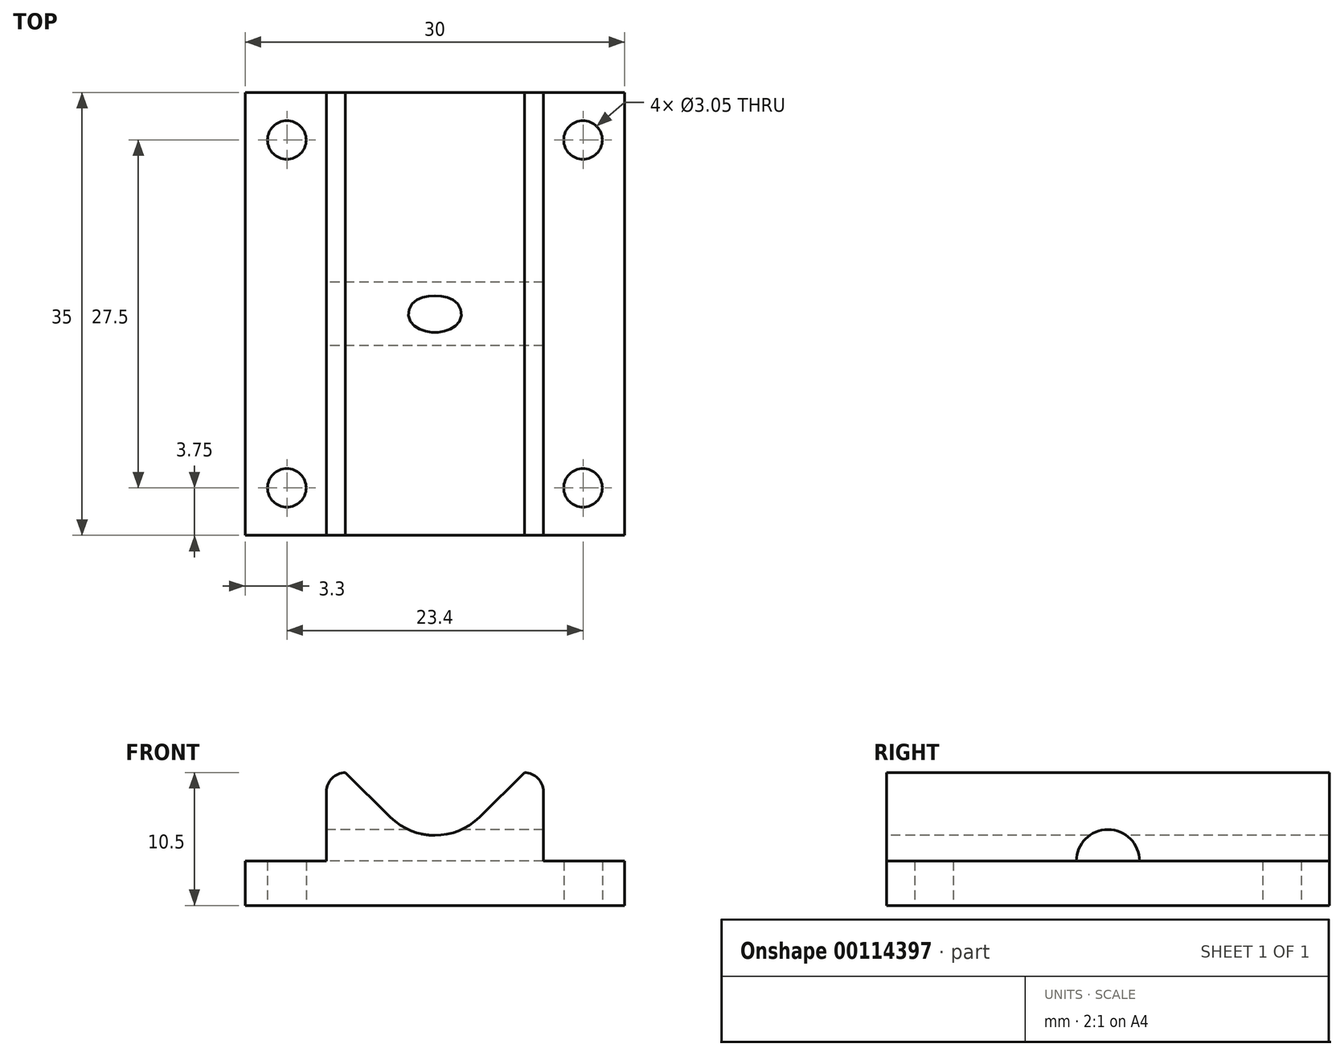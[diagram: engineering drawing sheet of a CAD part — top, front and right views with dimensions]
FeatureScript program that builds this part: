
annotation { "Feature Type Name" : "Feature", "Feature Type Description" : "" }
export const myFeature = defineFeature(function(context is Context, id is Id, definition is map)
    precondition{}
    {
        {
            var Q0;
            Q0=qCreatedBy(makeId("Top.planeOp"),FACE);
            var sketch = newSketch(context, id + "F0", { "sketchPlane" : qUnion([Q0])});
            skLineSegment(sketch, "E0.bottom", {"start": v(0, 0) * mm, "end": v(30, 0) * mm});
            skLineSegment(sketch, "E0.top", {"start": v(0, 35) * mm, "end": v(30, 35) * mm});
            skLineSegment(sketch, "E0.left", {"start": v(0, 0) * mm, "end": v(0, 35) * mm});
            skLineSegment(sketch, "E0.right", {"start": v(30, 0) * mm, "end": v(30, 35) * mm});
            skSolve(sketch);
        }
        {
            var Q0;
            Q0=makeQuery(id+"F0.imprint","IMPRINT",FACE,{"disambiguationData":[TD([[makeQuery(id+"F0.imprint","IMPRINT",EDGE,{"derivedFrom":sQuery(id+"F0.wireOp",EDGE,"E0.bottom")}),1.0]])]});
            extrude(context, id + "F1", {"entities" : qUnion([Q0]), "depth" : 13 * mm});
        }
        {
            var Q0;
            Q0=makeQuery(id+"F1.opExtrude","SWEPT_FACE",FACE,{"disambiguationData":[OSD([sQuery(id+"F0.wireOp",EDGE,"E0.bottom")])]});
            var sketch = newSketch(context, id + "F2", { "sketchPlane" : qUnion([Q0])});
            skLineSegment(sketch, "E1", {"start": v(15, 13) * mm, "end": v(15, 0) * mm, "construction": true});
            skCircle(sketch, "E2", {"center": v(15, 13) * mm, "radius": 6.75 * mm, "construction": true});
            skLineSegment(sketch, "E3", {"start": v(0, 3.5) * mm, "end": v(3.9, 3.5) * mm});
            skLineSegment(sketch, "E4", {"start": v(3.9, 3.5) * mm, "end": v(3.9, 13) * mm});
            skLineSegment(sketch, "E5", {"start": v(3.9, 13) * mm, "end": v(0, 13) * mm});
            skLineSegment(sketch, "E6", {"start": v(0, 13) * mm, "end": v(0, 3.5) * mm});
            skLineSegment(sketch, "E7", {"start": v(3.9, 13) * mm, "end": v(5.4, 13) * mm, "construction": true});
            skLineSegment(sketch, "E8", {"start": v(5.4, 13) * mm, "end": v(15, 3.5) * mm});
            skLineSegment(sketch, "E9", {"start": v(15, 3.5) * mm, "end": v(3.9, 3.5) * mm, "construction": true});
            skLineSegment(sketch, "E10", {"start": v(5.4, 13) * mm, "end": v(15, 13) * mm});
            skLineSegment(sketch, "E11", {"start": v(15, 3.5) * mm, "end": v(15, 13) * mm, "construction": true});
            skLineSegment(sketch, "E12.MirrorCS", {"start": v(15, 13) * mm, "end": v(15, 26) * mm, "construction": true});
            skLineSegment(sketch, "E13.MirrorCS", {"start": v(24.6, 13) * mm, "end": v(15, 13) * mm});
            skLineSegment(sketch, "E14.MirrorCS", {"start": v(24.6, 13) * mm, "end": v(15, 3.5) * mm});
            skLineSegment(sketch, "E15.MirrorCS", {"start": v(26.1, 3.5) * mm, "end": v(26.1, 13) * mm});
            skLineSegment(sketch, "E16.MirrorCS", {"start": v(26.1, 13) * mm, "end": v(30, 13) * mm});
            skLineSegment(sketch, "E17.MirrorCS", {"start": v(30, 13) * mm, "end": v(30, 3.5) * mm});
            skLineSegment(sketch, "E18.MirrorCS", {"start": v(30, 3.5) * mm, "end": v(26.1, 3.5) * mm});
            skLineSegment(sketch, "E19.MirrorCS", {"start": v(15, 3.5) * mm, "end": v(26.1, 3.5) * mm, "construction": true});
            skLineSegment(sketch, "E20.MirrorCS", {"start": v(26.1, 13) * mm, "end": v(24.6, 13) * mm, "construction": true});
            skSolve(sketch);
        }
        {
            var Q0;
            Q0=makeQuery(id+"F2.imprint","IMPRINT",FACE,{"disambiguationData":[TD([[makeQuery(id+"F2.imprint","IMPRINT",EDGE,{"derivedFrom":sQuery(id+"F2.wireOp",EDGE,"E3")}),1.0]])]});
            var Q1;
            Q1=makeQuery(id+"F2.imprint","IMPRINT",FACE,{"disambiguationData":[TD([[makeQuery(id+"F2.imprint","IMPRINT",EDGE,{"derivedFrom":sQuery(id+"F2.wireOp",EDGE,"E8")}),1.0]])]});
            var Q2;
            Q2=makeQuery(id+"F2.imprint","IMPRINT",FACE,{"disambiguationData":[TD([[makeQuery(id+"F2.imprint","IMPRINT",EDGE,{"derivedFrom":sQuery(id+"F2.wireOp",EDGE,"E15.MirrorCS")}),-1.0]])]});
            extrude(context, id + "F3", {"entities" : qUnion([Q0, Q1, Q2]), "operationType" : NewBodyOperationType.REMOVE, "endBound" : BoundingType.THROUGH_ALL, "oppositeDirection" : true, "depth" : 25 * mm});
        }
        {
            var Q0;
            {var subQ8=sQuery(id+"F2.wireOp",EDGE,"E3");Q0=makeQuery(id+"F2.imprint","IMPRINT",FACE,{"disambiguationData":[TD([[makeQuery(id+"F2.imprint","IMPRINT",EDGE,{"derivedFrom":subQ8}),-1.0]])]});}
            var sketch = newSketch(context, id + "F4", { "sketchPlane" : qUnion([Q0])});
            skLineSegment(sketch, "E21.0.0", {"start": v(3.9, 3.5) * mm, "end": v(0, 3.5) * mm, "construction": true});
            skLineSegment(sketch, "E21.0.1", {"start": v(0, 3.5) * mm, "end": v(0, 0) * mm, "construction": true});
            skLineSegment(sketch, "E21.0.2", {"start": v(0, 0) * mm, "end": v(30, 0) * mm, "construction": true});
            skLineSegment(sketch, "E21.0.3", {"start": v(30, 0) * mm, "end": v(30, 3.5) * mm, "construction": true});
            skLineSegment(sketch, "E21.0.4", {"start": v(30, 3.5) * mm, "end": v(26.1, 3.5) * mm, "construction": true});
            skLineSegment(sketch, "E21.0.5", {"start": v(26.1, 3.5) * mm, "end": v(26.1, 13) * mm});
            skLineSegment(sketch, "E21.0.6", {"start": v(26.1, 13) * mm, "end": v(24.6, 13) * mm});
            skLineSegment(sketch, "E21.0.7", {"start": v(24.6, 13) * mm, "end": v(15, 3.5) * mm});
            skLineSegment(sketch, "E21.0.8", {"start": v(15, 3.5) * mm, "end": v(5.4, 13) * mm});
            skLineSegment(sketch, "E21.0.9", {"start": v(5.4, 13) * mm, "end": v(3.9, 13) * mm});
            skLineSegment(sketch, "E21.0.10", {"start": v(3.9, 13) * mm, "end": v(3.9, 3.5) * mm});
            skLineSegment(sketch, "E22", {"start": v(3.9, 10.5) * mm, "end": v(7.93, 10.5) * mm});
            skLineSegment(sketch, "E23", {"start": v(15, 3.5) * mm, "end": v(15, 0) * mm, "construction": true});
            skLineSegment(sketch, "E24.MirrorCS", {"start": v(26.1, 10.5) * mm, "end": v(22.07, 10.5) * mm});
            skLineSegment(sketch, "E25", {"start": v(6.43, 10.5) * mm, "end": v(6.43, 3.5) * mm});
            skLineSegment(sketch, "E26", {"start": v(6.43, 3.5) * mm, "end": v(3.9, 3.5) * mm});
            skLineSegment(sketch, "E27.MirrorCS", {"start": v(23.57, 10.5) * mm, "end": v(23.57, 3.5) * mm});
            skLineSegment(sketch, "E28.MirrorCS", {"start": v(23.57, 3.5) * mm, "end": v(26.1, 3.5) * mm});
            skSolve(sketch);
        }
        {
            var Q0;
            {var subQ0=sQuery(id+"F4.wireOp",EDGE,"E21.0.9");Q0=makeQuery(id+"F4.imprint","IMPRINT",FACE,{"disambiguationData":[TD([[makeQuery(id+"F4.imprint","IMPRINT",EDGE,{"derivedFrom":subQ0}),-1.0]])]});}
            var Q1;
            {var subQ0=sQuery(id+"F4.wireOp",EDGE,"E21.0.6");Q1=makeQuery(id+"F4.imprint","IMPRINT",FACE,{"disambiguationData":[TD([[makeQuery(id+"F4.imprint","IMPRINT",EDGE,{"derivedFrom":subQ0}),-1.0]])]});}
            var Q2;
            {var subQ4=sQuery(id+"F4.wireOp",EDGE,"E25");Q2=makeQuery(id+"F4.imprint","IMPRINT",FACE,{"disambiguationData":[TD([[makeQuery(id+"F4.imprint","IMPRINT",EDGE,{"derivedFrom":subQ4}),-1.0]])]});}
            var Q3;
            {var subQ4=sQuery(id+"F4.wireOp",EDGE,"E27.MirrorCS");Q3=makeQuery(id+"F4.imprint","IMPRINT",FACE,{"disambiguationData":[TD([[makeQuery(id+"F4.imprint","IMPRINT",EDGE,{"derivedFrom":subQ4}),1.0]])]});}
            extrude(context, id + "F5", {"entities" : qUnion([Q0, Q1, Q2, Q3]), "operationType" : NewBodyOperationType.REMOVE, "endBound" : BoundingType.THROUGH_ALL, "oppositeDirection" : true, "depth" : 25 * mm});
        }
        {
            var Q0;
            Q0=makeQuery(id+"F3.boolean.opBoolean","COPY",EDGE,{"derivedFrom":makeQuery(id+"F3.opExtrude","SWEPT_EDGE",EDGE,{"disambiguationData":[OSD([sQuery(id+"F2.wireOp",EDGE,"E8"),sQuery(id+"F2.wireOp",EDGE,"E14.MirrorCS")])]})});
            fillet(context, id + "F6", {"entities" : qUnion([Q0]), "radius" : 5 * mm, "tangentPropagation" : true, "allowEdgeOverflow" : false});
        }
        {
            var Q0;
            Q0=makeQuery(id+"F1.opExtrude","SWEPT_FACE",FACE,{"disambiguationData":[OSD([sQuery(id+"F0.wireOp",EDGE,"E0.left")])]});
            var sketch = newSketch(context, id + "F7", { "sketchPlane" : qUnion([Q0])});
            skLineSegment(sketch, "E29.0", {"start": v(-35, 3.5) * mm, "end": v(0, 3.5) * mm});
            skArc(sketch, "E30", {"start": v(-15, 3.5) * mm, "mid": v(-17.5, 6) * mm, "end": v(-20, 3.5) * mm});
            skSolve(sketch);
        }
        {
            var Q0;
            Q0 = qSketchRegion(id + "F7", true);
            extrude(context, id + "F8", {"entities" : qUnion([Q0]), "operationType" : NewBodyOperationType.REMOVE, "endBound" : BoundingType.THROUGH_ALL, "oppositeDirection" : true, "depth" : 25 * mm});
        }
        {
            var Q0;
            Q0=makeQuery(id+"F1.opExtrude","CAP_FACE",FACE,{"disambiguationData":[OSD([sQuery(id+"F0.wireOp",EDGE,"E0.bottom"),sQuery(id+"F0.wireOp",EDGE,"E0.top"),sQuery(id+"F0.wireOp",EDGE,"E0.left"),sQuery(id+"F0.wireOp",EDGE,"E0.right")])],"isStart":true});
            var sketch = newSketch(context, id + "F9", { "sketchPlane" : qUnion([Q0])});
            skLineSegment(sketch, "E31.bottom", {"start": v(3.3, -3.75) * mm, "end": v(26.7, -3.75) * mm, "construction": true});
            skLineSegment(sketch, "E31.top", {"start": v(3.3, -31.25) * mm, "end": v(26.7, -31.25) * mm, "construction": true});
            skLineSegment(sketch, "E31.left", {"start": v(3.3, -3.75) * mm, "end": v(3.3, -31.25) * mm, "construction": true});
            skLineSegment(sketch, "E31.right", {"start": v(26.7, -3.75) * mm, "end": v(26.7, -31.25) * mm, "construction": true});
            skLineSegment(sketch, "E32", {"start": v(15, 0) * mm, "end": v(15, -35) * mm, "construction": true});
            skPoint(sketch, "E33", {"position": v(15, -3.75) * mm});
            skPoint(sketch, "E34", {"position": v(3.3, -17.5) * mm});
            skLineSegment(sketch, "E35", {"start": v(0, -17.5) * mm, "end": v(30, -17.5) * mm, "construction": true});
            skCircle(sketch, "E36", {"center": v(3.3, -3.75) * mm, "radius": 1.52 * mm});
            skCircle(sketch, "E37.MirrorC", {"center": v(26.7, -3.75) * mm, "radius": 1.52 * mm});
            skCircle(sketch, "E38.MirrorC", {"center": v(3.3, -31.25) * mm, "radius": 1.52 * mm});
            skCircle(sketch, "E39.MirrorC", {"center": v(26.7, -31.25) * mm, "radius": 1.52 * mm});
            skSolve(sketch);
        }
        {
            var Q0;
            Q0 = qSketchRegion(id + "F9", true);
            extrude(context, id + "F10", {"entities" : qUnion([Q0]), "operationType" : NewBodyOperationType.REMOVE, "endBound" : BoundingType.THROUGH_ALL, "oppositeDirection" : true, "depth" : 25 * mm});
        }
        {
            var Q0;
            Q0=makeQuery(id+"F5.boolean.opBoolean","COPY",EDGE,{"derivedFrom":makeQuery(id+"F5.opExtrude","SWEPT_EDGE",EDGE,{"disambiguationData":[OSD([sQuery(id+"F4.wireOp",EDGE,"E22"),sQuery(id+"F4.wireOp",EDGE,"E25")])]})});
            var Q1;
            Q1=makeQuery(id+"F5.boolean.opBoolean","COPY",EDGE,{"derivedFrom":makeQuery(id+"F5.opExtrude","SWEPT_EDGE",EDGE,{"disambiguationData":[OSD([sQuery(id+"F4.wireOp",EDGE,"E21.0.7"),sQuery(id+"F4.wireOp",EDGE,"E24.MirrorCS")])]})});
            var Q2;
            Q2=makeQuery(id+"F5.boolean.opBoolean","COPY",EDGE,{"derivedFrom":makeQuery(id+"F5.opExtrude","SWEPT_EDGE",EDGE,{"disambiguationData":[OSD([sQuery(id+"F4.wireOp",EDGE,"E24.MirrorCS"),sQuery(id+"F4.wireOp",EDGE,"E27.MirrorCS")])]})});
            fillet(context, id + "F11", {"entities" : qUnion([Q0, Q1, Q2]), "radius" : 1.5 * mm, "tangentPropagation" : true, "allowEdgeOverflow" : false});
        }
    });
